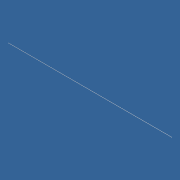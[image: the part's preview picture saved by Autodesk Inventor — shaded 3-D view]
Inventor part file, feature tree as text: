
AUTODESK INVENTOR PART (.ipt)
format: ipt  version: unknown  size: 157,184 bytes
history: native  units: in
note: dims shown in document units (in); Inventor stores cm internally (conversion verified against a paired STEP export)
features: revolve x1, sketch x1
ambient origin geometry x8: Origin, YZ Plane, XZ Plane, XY Plane, X Axis, Y Axis, Z Axis, Center Point
bodies: Solid1 (feature_tree)
feature tree (2):
  revolve  "Revolution1"  [1 undecoded]
  sketch  "Sketch1"  dims[d0=12.0in d1=0.01in d2=90.0deg]
note: 1 required parameter value undecoded (feature->parameter linkage not recoverable at this tier; creation-order binding heuristic only, values carry confidence <= 0.55)
